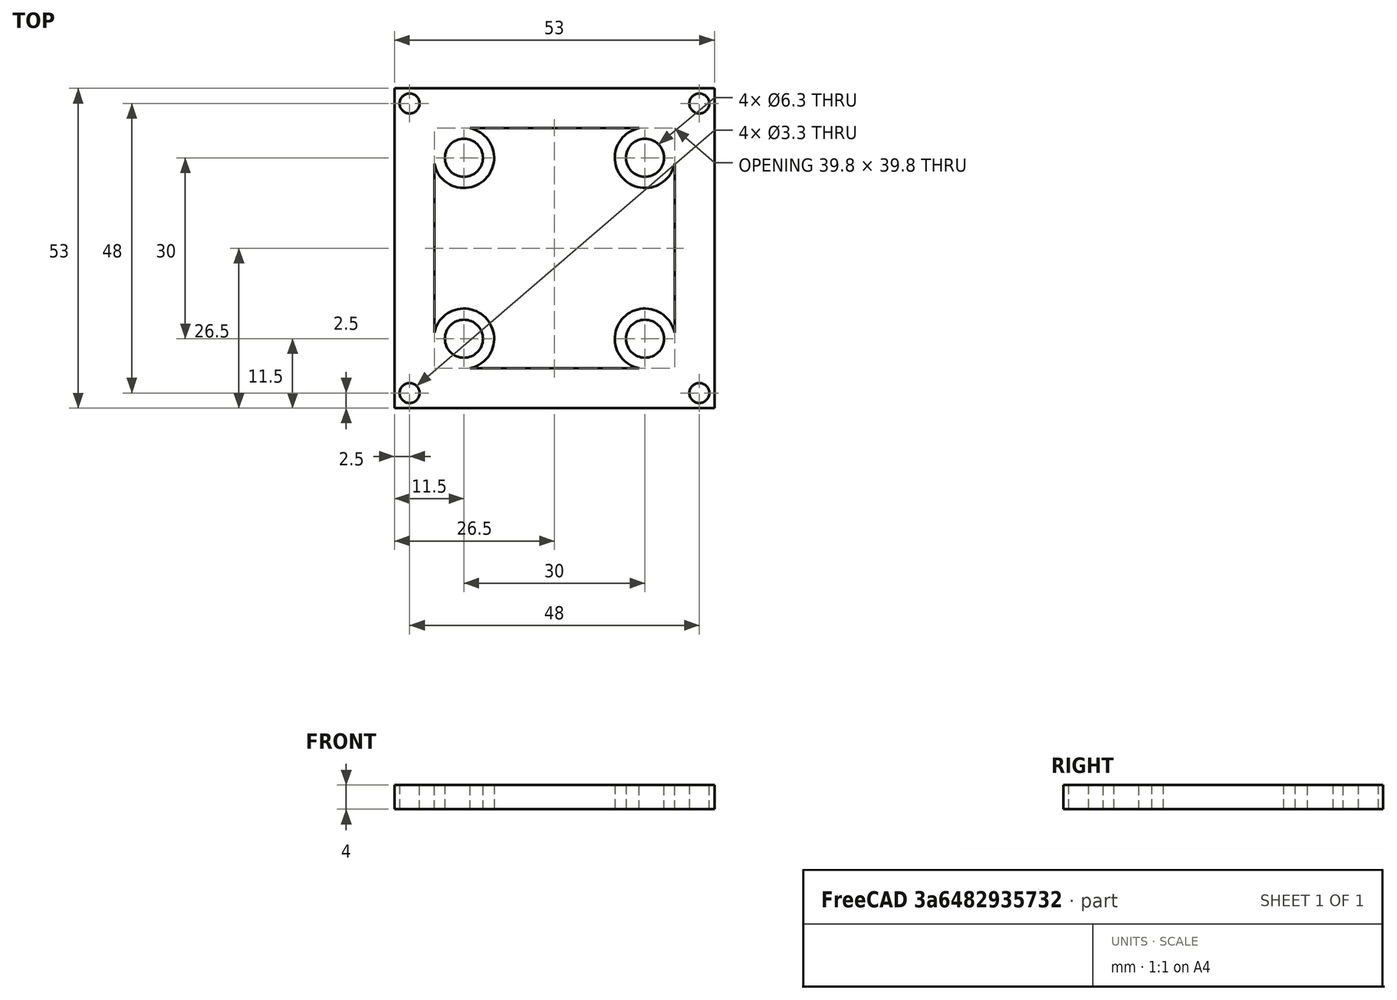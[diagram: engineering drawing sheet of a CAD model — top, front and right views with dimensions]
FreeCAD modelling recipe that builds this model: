
FCSTD DOCUMENT  (FreeCAD 0.18.4R)
Label: bracket
License: All rights reserved
LicenseURL: http://en.wikipedia.org/wiki/All_rights_reserved
objects: App::VRMLObject×1, Sketcher::SketchObject×1, PartDesign::Pad×1, PartDesign::Body×1
note: 4 computed .brp shape members not serialized (recipe doc carries the construction recipe); baked Part::Feature solids carry a one-line shape summary decoded from their .brp

FEATURE [App::VRMLObject] ambient
FEATURE [Sketcher::SketchObject] Sketch
  MapMode = 5
  Support = -> [XY_Plane]
  sketch-geometry (29):
    g0: LineSegment StartX=0 StartY=0 StartZ=0 EndX=53 EndY=0 EndZ=0
    g1: LineSegment StartX=53 StartY=0 StartZ=0 EndX=53 EndY=-53 EndZ=0
    g2: LineSegment StartX=53 StartY=-53 StartZ=0 EndX=0 EndY=-53 EndZ=0
    g3: LineSegment StartX=0 StartY=-53 StartZ=0 EndX=0 EndY=0 EndZ=0
    g4: Circle CenterX=2.5 CenterY=-2.5 CenterZ=0 NormalX=0 NormalY=0 NormalZ=1 AngleXU=0 Radius=1.65
    g5: Circle CenterX=50.5 CenterY=-2.5 CenterZ=0 NormalX=0 NormalY=0 NormalZ=1 AngleXU=0 Radius=1.65
    g6: Circle CenterX=50.5 CenterY=-50.5 CenterZ=0 NormalX=0 NormalY=0 NormalZ=1 AngleXU=0 Radius=1.65
    g7: Circle CenterX=2.5 CenterY=-50.5 CenterZ=0 NormalX=0 NormalY=0 NormalZ=1 AngleXU=0 Radius=1.65
    g8: LineSegment [constr] StartX=2.5 StartY=-2.5 StartZ=0 EndX=50.5 EndY=-2.5 EndZ=0
    g9: LineSegment [constr] StartX=50.5 StartY=-2.5 StartZ=0 EndX=50.5 EndY=-50.5 EndZ=0
    g10: LineSegment [constr] StartX=50.5 StartY=-50.5 StartZ=0 EndX=2.5 EndY=-50.5 EndZ=0
    g11: LineSegment [constr] StartX=2.5 StartY=-50.5 StartZ=0 EndX=2.5 EndY=-2.5 EndZ=0
    g12: GeomPoint X=26.5 Y=-26.5 Z=0
    g13: LineSegment [constr] StartX=11.5 StartY=-11.5 StartZ=0 EndX=41.5 EndY=-11.5 EndZ=0
    g14: LineSegment [constr] StartX=41.5 StartY=-11.5 StartZ=0 EndX=41.5 EndY=-41.5 EndZ=0
    g15: LineSegment [constr] StartX=41.5 StartY=-41.5 StartZ=0 EndX=11.5 EndY=-41.5 EndZ=0
    g16: LineSegment [constr] StartX=11.5 StartY=-41.5 StartZ=0 EndX=11.5 EndY=-11.5 EndZ=0
    g17: Circle CenterX=11.5 CenterY=-11.5 CenterZ=0 NormalX=0 NormalY=0 NormalZ=1 AngleXU=0 Radius=3.15
    g18: Circle CenterX=41.5 CenterY=-11.5 CenterZ=0 NormalX=0 NormalY=0 NormalZ=1 AngleXU=0 Radius=3.15
    g19: Circle CenterX=41.5 CenterY=-41.5 CenterZ=0 NormalX=0 NormalY=0 NormalZ=1 AngleXU=0 Radius=3.15
    g20: Circle CenterX=11.5 CenterY=-41.5 CenterZ=0 NormalX=0 NormalY=0 NormalZ=1 AngleXU=0 Radius=3.15
    g21: ArcOfCircle CenterX=11.5 CenterY=-11.5 CenterZ=0 NormalX=0 NormalY=0 NormalZ=1 AngleXU=0 Radius=5 StartAngle=3.34295 EndAngle=7.65262
    g22: ArcOfCircle CenterX=41.5 CenterY=-11.5 CenterZ=0 NormalX=0 NormalY=0 NormalZ=1 AngleXU=0 Radius=5 StartAngle=1.77215 EndAngle=6.08183
    g23: ArcOfCircle CenterX=41.5 CenterY=-41.5 CenterZ=0 NormalX=0 NormalY=0 NormalZ=1 AngleXU=0 Radius=5 StartAngle=0.201358 EndAngle=4.51103
    g24: ArcOfCircle CenterX=11.5 CenterY=-41.5 CenterZ=0 NormalX=0 NormalY=0 NormalZ=1 AngleXU=0 Radius=5 StartAngle=4.91375 EndAngle=9.22342
    g25: LineSegment StartX=6.60102 StartY=-12.5 StartZ=0 EndX=6.60102 EndY=-40.5 EndZ=0
    g26: LineSegment StartX=12.5 StartY=-46.399 StartZ=0 EndX=40.5 EndY=-46.399 EndZ=0
    g27: LineSegment StartX=46.399 StartY=-40.5 StartZ=0 EndX=46.399 EndY=-12.5 EndZ=0
    g28: LineSegment StartX=40.5 StartY=-6.60102 StartZ=0 EndX=12.5 EndY=-6.60102 EndZ=0
  constraints (75):
    c: Coincident(g0,g1)
    c: Coincident(g1,g2)
    c: Coincident(g2,g3)
    c: Coincident(g3,g0)
    c: Horizontal(g0)
    c: Horizontal(g2)
    c: Vertical(g1)
    c: Vertical(g3)
    c: Coincident(g0,g-1)
    c: Equal(g1,g2)
    c: Coincident(g8,g9)
    c: Coincident(g9,g10)
    c: Coincident(g10,g11)
    c: Coincident(g11,g8)
    c: Horizontal(g8)
    c: Horizontal(g10)
    c: Vertical(g9)
    c: Vertical(g11)
    c: Coincident(g8,g4)
    c: Coincident(g9,g6)
    c: Equal(g9,g8)
    c: Coincident(g5,g8)
    c: Coincident(g10,g7)
    c: Symmetric(g0,g1,g12)
    c: Symmetric(g4,g6,g12)
    c: Equal(g4,g5)
    c: Equal(g5,g6)
    c: Equal(g6,g7)
    c: DistanceX(g8,g8) = 48
    c: Diameter(g4) = 3.3
    c: DistanceX(g0,g0) = 53
    c: Coincident(g13,g14)
    c: Coincident(g14,g15)
    c: Coincident(g15,g16)
    c: Coincident(g16,g13)
    c: Horizontal(g13)
    c: Horizontal(g15)
    c: Vertical(g14)
    c: Vertical(g16)
    c: Equal(g13,g14)
    c: Symmetric(g13,g14,g12)
    c: DistanceX(g13,g13) = 30
    c: Coincident(g17,g13)
    c: Coincident(g18,g13)
    c: Coincident(g19,g14)
    c: Coincident(g20,g15)
    c: Equal(g17,g20)
    c: Equal(g20,g19)
    c: Equal(g19,g18)
    c: Diameter(g18) = 6.3
    c: Coincident(g21,g17)
    c: Coincident(g22,g18)
    c: Coincident(g23,g19)
    c: Coincident(g24,g20)
    c: Coincident(g25,g21)
    c: Coincident(g25,g24)
    c: Coincident(g26,g24)
    c: Coincident(g26,g23)
    c: Horizontal(g26)
    c: Coincident(g27,g23)
    c: Coincident(g27,g22)
    c: Vertical(g27)
    c: Coincident(g28,g22)
    c: Coincident(g28,g21)
    c: Horizontal(g28)
    c: Vertical(g25)
    c: Equal(g21,g22)
    c: Equal(g22,g23)
    c: Equal(g23,g24)
    c: Equal(g27,g25)
    c: DistanceY(g27,g27) = 28
    c: Radius(g21) = 5
    c: Equal(g28,g27)
    c: Equal(g27,g26)
    c: Equal(g26,g25)
FEATURE [PartDesign::Pad] Pad
  Length = 4
  Length2 = 100
  Profile = -> Sketch
  Type = 0
FEATURE [PartDesign::Body] Body
  Group = -> [Sketch,Pad]
  Origin = -> Origin
  Tip = -> Pad
